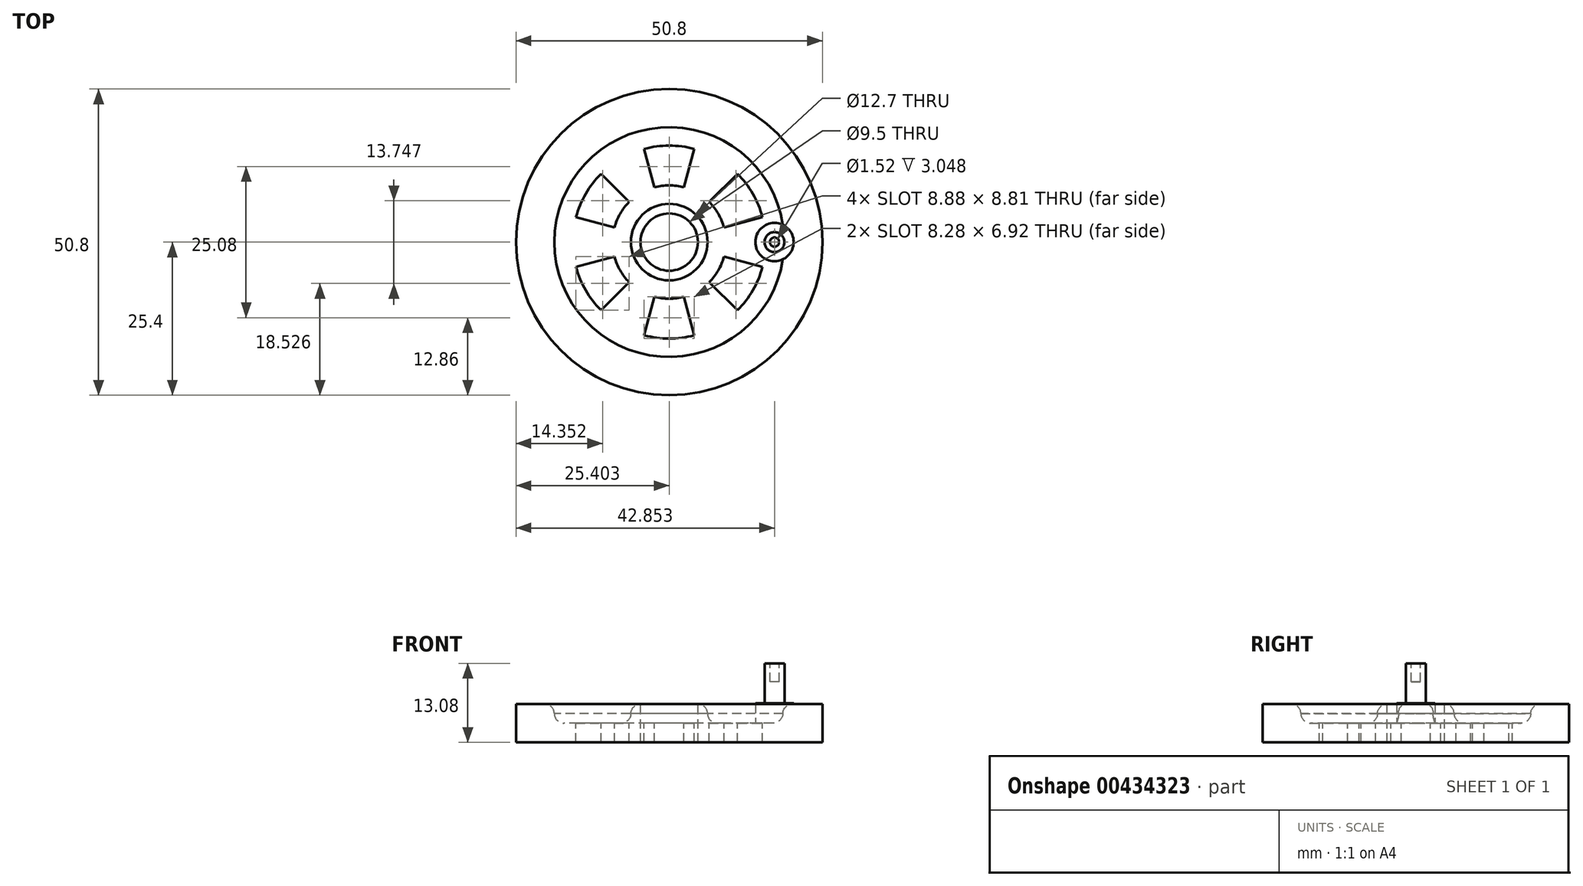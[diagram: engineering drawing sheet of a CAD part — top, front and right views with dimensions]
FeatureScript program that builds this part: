
annotation { "Feature Type Name" : "Feature", "Feature Type Description" : "" }
export const myFeature = defineFeature(function(context is Context, id is Id, definition is map)
    precondition{}
    {
        {
            var Q0;
            Q0=qCreatedBy(makeId("Front.planeOp"),FACE);
            var sketch = newSketch(context, id + "F0", { "sketchPlane" : qUnion([Q0])});
            skLineSegment(sketch, "E0", {"start": v(8.53, 0) * mm, "end": v(8.53, 6.35) * mm});
            skLineSegment(sketch, "E1", {"start": v(8.53, 6.35) * mm, "end": v(8.53, 6.35) * mm});
            skLineSegment(sketch, "E2", {"start": v(10.13, 4.78) * mm, "end": v(10.13, 4.75) * mm});
            skLineSegment(sketch, "E3", {"start": v(11.73, 3.18) * mm, "end": v(21.23, 3.18) * mm});
            skLineSegment(sketch, "E4", {"start": v(22.83, 4.75) * mm, "end": v(22.83, 4.78) * mm});
            skLineSegment(sketch, "E5", {"start": v(24.43, 6.35) * mm, "end": v(29.18, 6.35) * mm});
            skLineSegment(sketch, "E6", {"start": v(29.18, 6.35) * mm, "end": v(29.18, 0) * mm});
            skLineSegment(sketch, "E7", {"start": v(29.18, 0) * mm, "end": v(8.53, 0) * mm});
            skArc(sketch, "E8", {"start": v(29.18, 6.35) * mm, "mid": v(32.36, 3.18) * mm, "end": v(29.18, 0) * mm});
            skLineSegment(sketch, "E9", {"start": v(3.78, 8.27) * mm, "end": v(3.78, -3.55) * mm, "construction": true});
            skPoint(sketch, "E10.visualSharp", {"position": v(10.13, 6.35) * mm});
            skArc(sketch, "E10.filletArc", {"start": v(10.13, 4.75) * mm, "mid": v(9.66, 5.88) * mm, "end": v(8.53, 6.35) * mm});
            skPoint(sketch, "E11.visualSharp", {"position": v(10.13, 3.18) * mm});
            skArc(sketch, "E11.filletArc", {"start": v(10.13, 4.78) * mm, "mid": v(10.6, 3.64) * mm, "end": v(11.73, 3.18) * mm});
            skPoint(sketch, "E12.visualSharp", {"position": v(22.83, 6.35) * mm});
            skArc(sketch, "E12.filletArc", {"start": v(24.43, 6.35) * mm, "mid": v(23.3, 5.88) * mm, "end": v(22.83, 4.75) * mm});
            skPoint(sketch, "E13.visualSharp", {"position": v(22.83, 3.18) * mm});
            skArc(sketch, "E13.filletArc", {"start": v(21.23, 3.18) * mm, "mid": v(22.36, 3.64) * mm, "end": v(22.83, 4.78) * mm});
            skSolve(sketch);
        }
        {
            var Q0;
            Q0=makeQuery(id+"F0.imprint","IMPRINT",FACE,{"disambiguationData":[TD([[makeQuery(id+"F0.imprint","IMPRINT",EDGE,{"derivedFrom":sQuery(id+"F0.wireOp",EDGE,"E0")}),-1.0]])]});
            var Q1;
            Q1=sQuery(id+"F0.wireOp",EDGE,"E9");
            revolve(context, id + "F1", {"entities" : qUnion([Q0]), "axis" : qUnion([Q1]), "revolveType" : RevolveType.FULL});
        }
        {
            var Q0;
            Q0=makeQuery(id+"F1.opRevolve","SWEPT_FACE",FACE,{"disambiguationData":[OSD([sQuery(id+"F0.wireOp",EDGE,"E3")])]});
            var sketch = newSketch(context, id + "F2", { "sketchPlane" : qUnion([Q0])});
            skLineSegment(sketch, "E14", {"start": v(6.22, 9.08) * mm, "end": v(7.92, 15.46) * mm});
            skLineSegment(sketch, "E15.MirrorCS", {"start": v(1.35, 9.08) * mm, "end": v(-0.36, 15.46) * mm});
            skArc(sketch, "E16", {"start": v(7.92, 15.46) * mm, "mid": v(3.78, 16) * mm, "end": v(-0.36, 15.46) * mm});
            skArc(sketch, "E17", {"start": v(6.22, 9.08) * mm, "mid": v(3.78, 9.4) * mm, "end": v(1.35, 9.08) * mm});
            skPoint(sketch, "E18.orphan", {"position": v(-0.73, 16.86) * mm});
            skPoint(sketch, "E19.orphan", {"position": v(8.3, 16.86) * mm});
            skArc(sketch, "E20.1.0", {"start": v(-7.53, 11.32) * mm, "mid": v(-10.08, 8) * mm, "end": v(-11.67, 4.14) * mm});
            skLineSegment(sketch, "E20.1.1", {"start": v(-5.3, 2.43) * mm, "end": v(-11.67, 4.14) * mm});
            skArc(sketch, "E20.1.2", {"start": v(-2.86, 6.65) * mm, "mid": v(-4.36, 4.7) * mm, "end": v(-5.3, 2.43) * mm});
            skLineSegment(sketch, "E20.1.3", {"start": v(-2.86, 6.65) * mm, "end": v(-7.53, 11.32) * mm});
            skArc(sketch, "E20.2.0", {"start": v(-11.67, -4.14) * mm, "mid": v(-10.08, -8) * mm, "end": v(-7.53, -11.32) * mm});
            skLineSegment(sketch, "E20.2.1", {"start": v(-2.86, -6.65) * mm, "end": v(-7.53, -11.32) * mm});
            skArc(sketch, "E20.2.2", {"start": v(-5.3, -2.43) * mm, "mid": v(-4.36, -4.7) * mm, "end": v(-2.86, -6.65) * mm});
            skLineSegment(sketch, "E20.2.3", {"start": v(-5.3, -2.43) * mm, "end": v(-11.67, -4.14) * mm});
            skArc(sketch, "E20.3.0", {"start": v(-0.36, -15.46) * mm, "mid": v(3.78, -16) * mm, "end": v(7.92, -15.46) * mm});
            skLineSegment(sketch, "E20.3.1", {"start": v(6.22, -9.08) * mm, "end": v(7.92, -15.46) * mm});
            skArc(sketch, "E20.3.2", {"start": v(1.35, -9.08) * mm, "mid": v(3.78, -9.4) * mm, "end": v(6.22, -9.08) * mm});
            skLineSegment(sketch, "E20.3.3", {"start": v(1.35, -9.08) * mm, "end": v(-0.36, -15.46) * mm});
            skArc(sketch, "E20.4.0", {"start": v(15.1, -11.32) * mm, "mid": v(17.64, -8) * mm, "end": v(19.24, -4.14) * mm});
            skLineSegment(sketch, "E20.4.1", {"start": v(12.86, -2.43) * mm, "end": v(19.24, -4.14) * mm});
            skArc(sketch, "E20.4.2", {"start": v(10.43, -6.65) * mm, "mid": v(11.92, -4.7) * mm, "end": v(12.86, -2.43) * mm});
            skLineSegment(sketch, "E20.4.3", {"start": v(10.43, -6.65) * mm, "end": v(15.1, -11.32) * mm});
            skArc(sketch, "E21.1.5.0", {"start": v(19.24, 4.14) * mm, "mid": v(17.64, 8) * mm, "end": v(15.1, 11.32) * mm});
            skLineSegment(sketch, "E21.4.5.0", {"start": v(10.43, 6.65) * mm, "end": v(15.1, 11.32) * mm});
            skArc(sketch, "E21.7.5.0", {"start": v(12.86, 2.43) * mm, "mid": v(11.92, 4.7) * mm, "end": v(10.43, 6.65) * mm});
            skLineSegment(sketch, "E21.11.5.0", {"start": v(12.86, 2.43) * mm, "end": v(19.24, 4.14) * mm});
            skSolve(sketch);
        }
        {
            var Q0;
            Q0=makeQuery(id+"F2.imprint","IMPRINT",FACE,{"disambiguationData":[TD([[makeQuery(id+"F2.imprint","IMPRINT",EDGE,{"derivedFrom":sQuery(id+"F2.wireOp",EDGE,"E14")}),1.0]])]});
            var Q1;
            Q1=makeQuery(id+"F2.imprint","IMPRINT",FACE,{"disambiguationData":[TD([[makeQuery(id+"F2.imprint","IMPRINT",EDGE,{"derivedFrom":sQuery(id+"F2.wireOp",EDGE,"E20.1.0")}),1.0]])]});
            var Q2;
            Q2=makeQuery(id+"F2.imprint","IMPRINT",FACE,{"disambiguationData":[TD([[makeQuery(id+"F2.imprint","IMPRINT",EDGE,{"derivedFrom":sQuery(id+"F2.wireOp",EDGE,"E20.2.0")}),1.0]])]});
            var Q3;
            Q3=makeQuery(id+"F2.imprint","IMPRINT",FACE,{"disambiguationData":[TD([[makeQuery(id+"F2.imprint","IMPRINT",EDGE,{"derivedFrom":sQuery(id+"F2.wireOp",EDGE,"E20.3.0")}),1.0]])]});
            var Q4;
            Q4=makeQuery(id+"F2.imprint","IMPRINT",FACE,{"disambiguationData":[TD([[makeQuery(id+"F2.imprint","IMPRINT",EDGE,{"derivedFrom":sQuery(id+"F2.wireOp",EDGE,"E20.4.0")}),1.0]])]});
            var Q5;
            Q5=makeQuery(id+"F2.imprint","IMPRINT",FACE,{"disambiguationData":[TD([[makeQuery(id+"F2.imprint","IMPRINT",EDGE,{"derivedFrom":sQuery(id+"F2.wireOp",EDGE,"E21.1.5.0")}),1.0]])]});
            extrude(context, id + "F3", {"entities" : qUnion([Q0, Q1, Q2, Q3, Q4, Q5]), "operationType" : NewBodyOperationType.REMOVE, "oppositeDirection" : true, "depth" : 25.4 * mm});
        }
        {
            var Q0;
            Q0=makeQuery(id+"F1.opRevolve","SWEPT_BODY",BODY,{"disambiguationData":[OSD([sQuery(id+"F0.wireOp",EDGE,"E0"),sQuery(id+"F0.wireOp",EDGE,"E2"),sQuery(id+"F0.wireOp",EDGE,"E3"),sQuery(id+"F0.wireOp",EDGE,"E4"),sQuery(id+"F0.wireOp",EDGE,"E5"),sQuery(id+"F0.wireOp",EDGE,"E6"),sQuery(id+"F0.wireOp",EDGE,"E7"),sQuery(id+"F0.wireOp",EDGE,"E10.filletArc"),sQuery(id+"F0.wireOp",EDGE,"E11.filletArc"),sQuery(id+"F0.wireOp",EDGE,"E12.filletArc"),sQuery(id+"F0.wireOp",EDGE,"E13.filletArc")])]});
            var Q1;
            Q1=makeQuery(id+"F1.opRevolve","SWEPT_EDGE",EDGE,{"disambiguationData":[OSD([sQuery(id+"F0.wireOp",EDGE,"E5"),sQuery(id+"F0.wireOp",EDGE,"E6"),sQuery(id+"F0.wireOp",EDGE,"E8")])]});
            var Q2;
            Q2=qCreatedBy(makeId("Right.planeOp"),FACE);
            transform(context, id + "F4", {"entities" : qUnion([Q0]), "transformType" : TransformType.TRANSLATION_DISTANCE, "transformDirection" : qUnion([Q2]), "distance" : 3.8 * mm, "oppositeDirection" : true, "makeCopy" : false});
        }
        {
            var Q0;
            Q0=makeQuery(id+"F1.opRevolve","SWEPT_FACE",FACE,{"disambiguationData":[OSD([sQuery(id+"F0.wireOp",EDGE,"E3")])]});
            var sketch = newSketch(context, id + "F5", { "sketchPlane" : qUnion([Q0])});
            skCircle(sketch, "E22", {"center": v(17.42, 0) * mm, "radius": 3.18 * mm});
            skSolve(sketch);
        }
        {
            var Q0;
            Q0=qSketchRegion(id+"F5",true);
            extrude(context, id + "F6", {"entities" : qUnion([Q0]), "operationType" : NewBodyOperationType.ADD, "depth" : 3.3 * mm});
        }
        {
            var Q0;
            Q0=makeQuery(id+"F6.opExtrude","CAP_FACE",FACE,{"disambiguationData":[OSD([sQuery(id+"F5.wireOp",EDGE,"E22")])],"isStart":false});
            var sketch = newSketch(context, id + "F7", { "sketchPlane" : qUnion([Q0])});
            skCircle(sketch, "E23", {"center": v(17.42, 0) * mm, "radius": 1.65 * mm});
            skSolve(sketch);
        }
        {
            var Q0;
            Q0=makeQuery(id+"F7.imprint","IMPRINT",FACE,{"disambiguationData":[TD([[makeQuery(id+"F7.imprint","IMPRINT",EDGE,{"derivedFrom":sQuery(id+"F7.wireOp",EDGE,"E23")}),1.0]])]});
            var Q1;
            Q1=sQuery(id+"F7.wireOp",EDGE,"E23");
            extrude(context, id + "F8", {"entities" : qUnion([Q0]), "surfaceEntities" : qUnion([Q1]), "depth" : 6.6 * mm});
        }
        {
            var Q0;
            Q0=makeQuery(id+"F8.opExtrude","CAP_FACE",FACE,{"disambiguationData":[OSD([sQuery(id+"F7.wireOp",EDGE,"E23")])],"isStart":false});
            var sketch = newSketch(context, id + "F9", { "sketchPlane" : qUnion([Q0])});
            skCircle(sketch, "E24", {"center": v(17.42, 0) * mm, "radius": 0.76 * mm});
            skSolve(sketch);
        }
        {
            var Q0;
            Q0=makeQuery(id+"F9.imprint","IMPRINT",FACE,{"disambiguationData":[TD([[makeQuery(id+"F9.imprint","IMPRINT",EDGE,{"derivedFrom":sQuery(id+"F9.wireOp",EDGE,"E24")}),1.0]])]});
            extrude(context, id + "F10", {"entities" : qUnion([Q0]), "operationType" : NewBodyOperationType.REMOVE, "oppositeDirection" : true, "depth" : 3.05 * mm});
        }
    });
